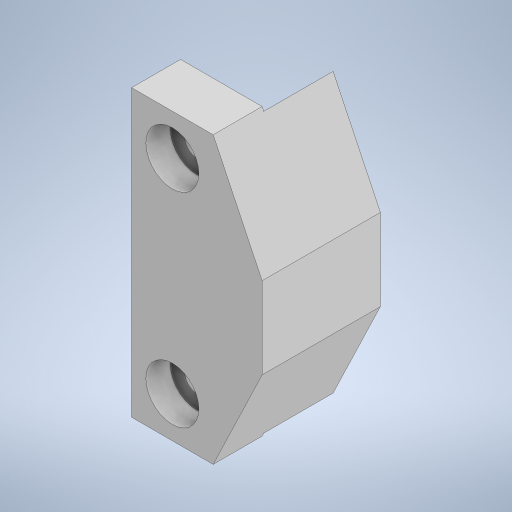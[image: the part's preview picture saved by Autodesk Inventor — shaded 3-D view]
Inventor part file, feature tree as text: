
AUTODESK INVENTOR PART (.ipt)
format: ipt  version: 2024 (Build 280153000, 153)  size: 293,376 bytes
history: native  units: mm
features: extrude x4, sketch x4, projected_geometry x4
ambient origin geometry x8: Origin, YZ Plane, XZ Plane, XY Plane, X Axis, Y Axis, Z Axis, Center Point
bodies: Solid1 (feature_tree)
feature tree (12):
  extrude  "Extrusion1"  Depth=25.0mm
  extrude  "Extrusion2"  Depth=10.0mm
  extrude  "Extrusion3"  Depth=3.0mm
  extrude  "Extrusion4"  Depth=6.0mm
  sketch  "Sketch1"  dims[d0=5.0mm d1=25.0mm]
  sketch  "Sketch2"  dims[d2=5.0mm d3=10.0mm]
  projected_geometry  "Projected Loop1"
  sketch  "Sketch3"  dims[d4=5.0mm d5=3.0mm]
  projected_geometry  "Projected Loop2"
  sketch  "Sketch4"  dims[d6=3.0mm d7=6.0mm d8=5.0mm d9=5.0mm d10=6.0mm d11=0.0mm d12=8.5mm d13=0.0mm d14=6.5mm d15=3.0mm d16=0.0mm d17=6.5mm d36=6.0mm d39=3.0mm d41=90.0deg d42=3.0mm d43=90.0deg d45=2.9mm d46=2.0mm d47=2.0mm d48=8.0mm d49=0.0mm d52=8.217909mm d54=0.2mm d55=2.9mm d56=0.2mm d57=6.0mm d53=0.5mm]
  projected_geometry  "Projected Loop3"
  projected_geometry  "Projected Loop4"
